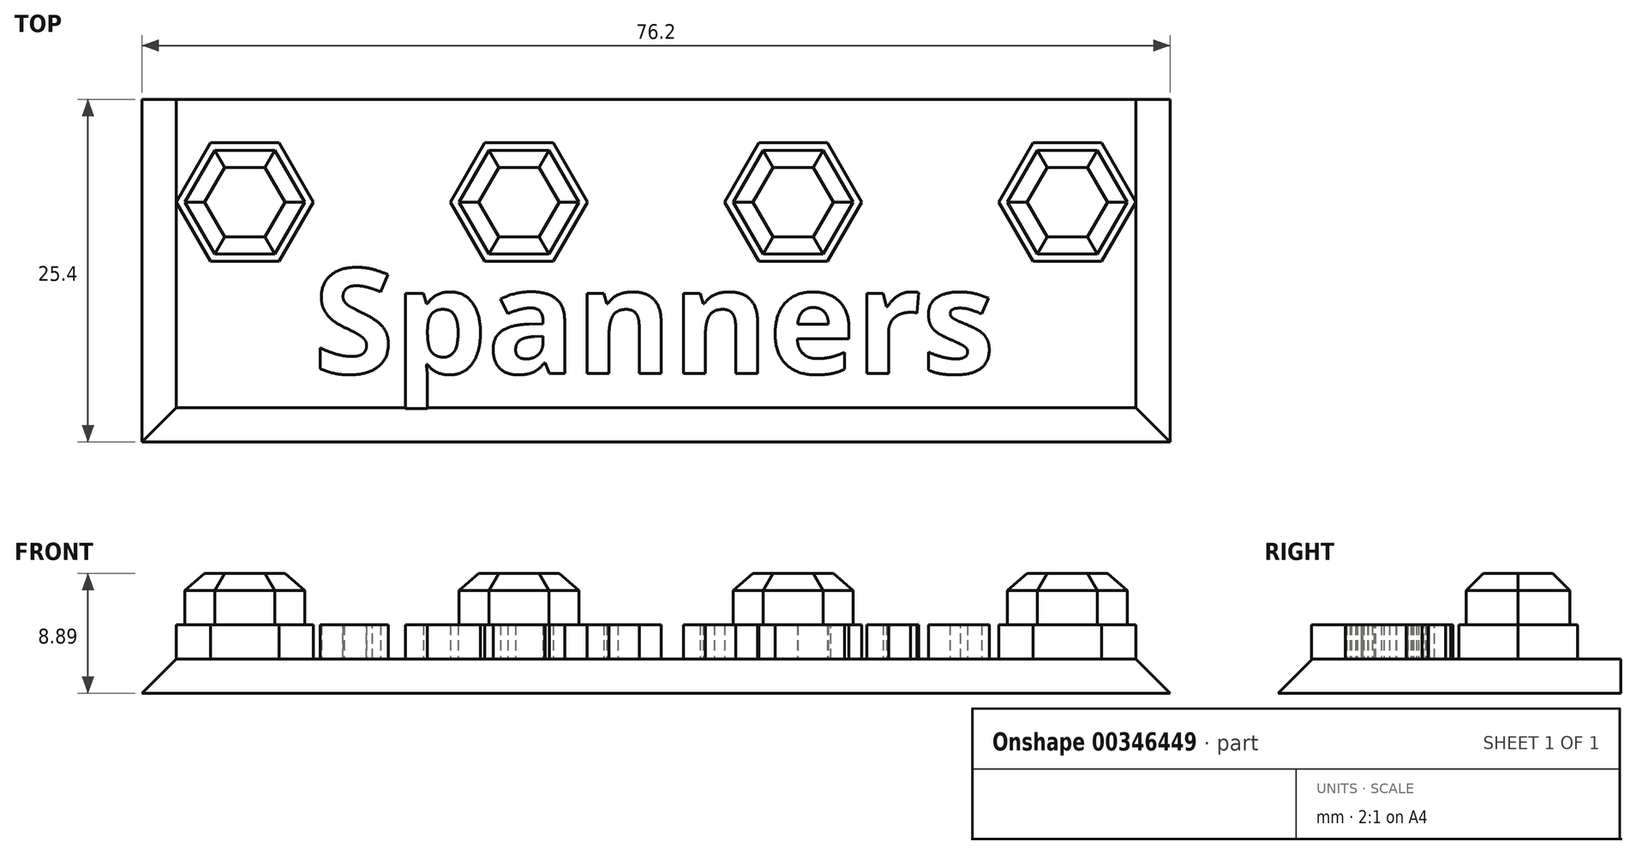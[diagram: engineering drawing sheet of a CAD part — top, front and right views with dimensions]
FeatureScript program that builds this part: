
annotation { "Feature Type Name" : "Feature", "Feature Type Description" : "" }
export const myFeature = defineFeature(function(context is Context, id is Id, definition is map)
    precondition{}
    {
        {
            var Q0;
            Q0=qCreatedBy(makeId("Top.planeOp"),FACE);
            var sketch = newSketch(context, id + "F0", { "sketchPlane" : qUnion([Q0])});
            skLineSegment(sketch, "E0.bottom", {"start": v(-52.82, 92.77) * mm, "end": v(23.38, 92.77) * mm});
            skLineSegment(sketch, "E0.top", {"start": v(-52.82, 67.37) * mm, "end": v(23.38, 67.37) * mm});
            skLineSegment(sketch, "E0.left", {"start": v(-52.82, 92.77) * mm, "end": v(-52.82, 67.37) * mm});
            skLineSegment(sketch, "E0.right", {"start": v(23.38, 92.77) * mm, "end": v(23.38, 67.37) * mm});
            skCircle(sketch, "E1.cCircle", {"center": v(-45.2, 85.15) * mm, "radius": 4.4 * mm, "construction": true});
            skLineSegment(sketch, "E1.0", {"start": v(-40.12, 85.15) * mm, "end": v(-42.66, 80.75) * mm});
            skLineSegment(sketch, "E1.1", {"start": v(-42.66, 80.75) * mm, "end": v(-47.74, 80.75) * mm});
            skLineSegment(sketch, "E1.2", {"start": v(-47.74, 80.75) * mm, "end": v(-50.28, 85.15) * mm});
            skLineSegment(sketch, "E1.3", {"start": v(-50.28, 85.15) * mm, "end": v(-47.74, 89.55) * mm});
            skLineSegment(sketch, "E1.4", {"start": v(-47.74, 89.55) * mm, "end": v(-42.66, 89.55) * mm});
            skLineSegment(sketch, "E1.5", {"start": v(-42.66, 89.55) * mm, "end": v(-40.12, 85.15) * mm});
            skPoint(sketch, "E1.0.midPoint", {"position": v(-41.39, 82.95) * mm});
            skLineSegment(sketch, "E2.1.0.0", {"start": v(-22.34, 89.55) * mm, "end": v(-19.8, 85.15) * mm});
            skLineSegment(sketch, "E2.1.0.1", {"start": v(-27.42, 89.55) * mm, "end": v(-22.34, 89.55) * mm});
            skLineSegment(sketch, "E2.1.0.2", {"start": v(-29.96, 85.15) * mm, "end": v(-27.42, 89.55) * mm});
            skLineSegment(sketch, "E2.1.0.3", {"start": v(-27.42, 80.75) * mm, "end": v(-29.96, 85.15) * mm});
            skLineSegment(sketch, "E2.1.0.4", {"start": v(-22.34, 80.75) * mm, "end": v(-27.42, 80.75) * mm});
            skLineSegment(sketch, "E2.1.0.5", {"start": v(-19.8, 85.15) * mm, "end": v(-22.34, 80.75) * mm});
            skLineSegment(sketch, "E2.2.0.0", {"start": v(-2.02, 89.55) * mm, "end": v(0.52, 85.15) * mm});
            skLineSegment(sketch, "E2.2.0.1", {"start": v(-7.1, 89.55) * mm, "end": v(-2.02, 89.55) * mm});
            skLineSegment(sketch, "E2.2.0.2", {"start": v(-9.64, 85.15) * mm, "end": v(-7.1, 89.55) * mm});
            skLineSegment(sketch, "E2.2.0.3", {"start": v(-7.1, 80.75) * mm, "end": v(-9.64, 85.15) * mm});
            skLineSegment(sketch, "E2.2.0.4", {"start": v(-2.02, 80.75) * mm, "end": v(-7.1, 80.75) * mm});
            skLineSegment(sketch, "E2.2.0.5", {"start": v(0.52, 85.15) * mm, "end": v(-2.02, 80.75) * mm});
            skLineSegment(sketch, "E2.3.0.0", {"start": v(18.3, 89.55) * mm, "end": v(20.84, 85.15) * mm});
            skLineSegment(sketch, "E2.3.0.1", {"start": v(13.22, 89.55) * mm, "end": v(18.3, 89.55) * mm});
            skLineSegment(sketch, "E2.3.0.2", {"start": v(10.68, 85.15) * mm, "end": v(13.22, 89.55) * mm});
            skLineSegment(sketch, "E2.3.0.3", {"start": v(13.22, 80.75) * mm, "end": v(10.68, 85.15) * mm});
            skLineSegment(sketch, "E2.3.0.4", {"start": v(18.3, 80.75) * mm, "end": v(13.22, 80.75) * mm});
            skLineSegment(sketch, "E2.3.0.5", {"start": v(20.84, 85.15) * mm, "end": v(18.3, 80.75) * mm});
            skLineSegment(sketch, "E2.direction1", {"start": v(-40.12, 85.15) * mm, "end": v(-19.8, 85.15) * mm, "construction": true});
            skSolve(sketch);
        }
        {
            var Q0;
            Q0=makeQuery(id+"F0.imprint","IMPRINT",FACE,{"disambiguationData":[TD([[makeQuery(id+"F0.imprint","IMPRINT",EDGE,{"derivedFrom":sQuery(id+"F0.wireOp",EDGE,"E0.bottom")}),-1.0]])]});
            extrude(context, id + "F1", {"entities" : qUnion([Q0]), "depth" : 2.54 * mm});
        }
        {
            var Q0;
            Q0=makeQuery(id+"F1.opExtrude","CAP_FACE",FACE,{"disambiguationData":[OSD([sQuery(id+"F0.wireOp",EDGE,"E0.bottom"),sQuery(id+"F0.wireOp",EDGE,"E0.top"),sQuery(id+"F0.wireOp",EDGE,"E0.left"),sQuery(id+"F0.wireOp",EDGE,"E0.right"),sQuery(id+"F0.wireOp",EDGE,"E1.0"),sQuery(id+"F0.wireOp",EDGE,"E1.1"),sQuery(id+"F0.wireOp",EDGE,"E1.2"),sQuery(id+"F0.wireOp",EDGE,"E1.3"),sQuery(id+"F0.wireOp",EDGE,"E1.4"),sQuery(id+"F0.wireOp",EDGE,"E1.5")])],"isStart":false});
            var sketch = newSketch(context, id + "F2", { "sketchPlane" : qUnion([Q0])});
            skLineSegment(sketch, "E3.0", {"start": v(-47.74, 89.55) * mm, "end": v(-42.66, 89.55) * mm});
            skLineSegment(sketch, "E3.1", {"start": v(-42.66, 89.55) * mm, "end": v(-40.12, 85.15) * mm});
            skLineSegment(sketch, "E3.2", {"start": v(-40.12, 85.15) * mm, "end": v(-42.66, 80.75) * mm});
            skLineSegment(sketch, "E3.3", {"start": v(-42.66, 80.75) * mm, "end": v(-47.74, 80.75) * mm});
            skLineSegment(sketch, "E3.4", {"start": v(-47.74, 80.75) * mm, "end": v(-50.28, 85.15) * mm});
            skLineSegment(sketch, "E3.5", {"start": v(-50.28, 85.15) * mm, "end": v(-47.74, 89.55) * mm});
            skLineSegment(sketch, "E4.0", {"start": v(-27.42, 89.55) * mm, "end": v(-22.34, 89.55) * mm});
            skLineSegment(sketch, "E4.1", {"start": v(-22.34, 89.55) * mm, "end": v(-19.8, 85.15) * mm});
            skLineSegment(sketch, "E4.2", {"start": v(-19.8, 85.15) * mm, "end": v(-22.34, 80.75) * mm});
            skLineSegment(sketch, "E4.3", {"start": v(-22.34, 80.75) * mm, "end": v(-27.42, 80.75) * mm});
            skLineSegment(sketch, "E4.4", {"start": v(-27.42, 80.75) * mm, "end": v(-29.96, 85.15) * mm});
            skLineSegment(sketch, "E4.5", {"start": v(-29.96, 85.15) * mm, "end": v(-27.42, 89.55) * mm});
            skLineSegment(sketch, "E5.0", {"start": v(-9.64, 85.15) * mm, "end": v(-7.1, 89.55) * mm});
            skLineSegment(sketch, "E5.1", {"start": v(-7.1, 89.55) * mm, "end": v(-2.02, 89.55) * mm});
            skLineSegment(sketch, "E5.2", {"start": v(-2.02, 89.55) * mm, "end": v(0.52, 85.15) * mm});
            skLineSegment(sketch, "E5.3", {"start": v(0.52, 85.15) * mm, "end": v(-2.02, 80.75) * mm});
            skLineSegment(sketch, "E5.4", {"start": v(-2.02, 80.75) * mm, "end": v(-7.1, 80.75) * mm});
            skLineSegment(sketch, "E5.5", {"start": v(-7.1, 80.75) * mm, "end": v(-9.64, 85.15) * mm});
            skLineSegment(sketch, "E6.0", {"start": v(18.3, 89.55) * mm, "end": v(20.84, 85.15) * mm});
            skLineSegment(sketch, "E6.1", {"start": v(20.84, 85.15) * mm, "end": v(18.3, 80.75) * mm});
            skLineSegment(sketch, "E6.2", {"start": v(18.3, 80.75) * mm, "end": v(13.22, 80.75) * mm});
            skLineSegment(sketch, "E6.3", {"start": v(13.22, 80.75) * mm, "end": v(10.68, 85.15) * mm});
            skLineSegment(sketch, "E6.4", {"start": v(10.68, 85.15) * mm, "end": v(13.22, 89.55) * mm});
            skLineSegment(sketch, "E6.5", {"start": v(13.22, 89.55) * mm, "end": v(18.3, 89.55) * mm});
            skSolve(sketch);
        }
        {
            var Q0;
            Q0 = qSketchRegion(id + "F2", true);
            var Q1;
            Q1=makeQuery(id+"F1.opExtrude","CAP_FACE",FACE,{"disambiguationData":[OSD([sQuery(id+"F0.wireOp",EDGE,"E0.bottom"),sQuery(id+"F0.wireOp",EDGE,"E0.top"),sQuery(id+"F0.wireOp",EDGE,"E0.left"),sQuery(id+"F0.wireOp",EDGE,"E0.right"),sQuery(id+"F0.wireOp",EDGE,"E1.0"),sQuery(id+"F0.wireOp",EDGE,"E1.1"),sQuery(id+"F0.wireOp",EDGE,"E1.2"),sQuery(id+"F0.wireOp",EDGE,"E1.3"),sQuery(id+"F0.wireOp",EDGE,"E1.4"),sQuery(id+"F0.wireOp",EDGE,"E1.5")])],"isStart":true});
            extrude(context, id + "F3", {"entities" : qUnion([Q0]), "operationType" : NewBodyOperationType.ADD, "depth" : 2.54 * mm, "hasSecondDirection" : true, "secondDirectionBound" : SecondDirectionBoundingType.UP_TO_SURFACE, "secondDirectionOppositeDirection" : true, "secondDirectionBoundEntityFace" : qUnion([Q1]), "secondDirectionDepth" : 25.4 * mm});
        }
        {
            var Q0;
            Q0=makeQuery(id+"F3.opExtrude","CAP_FACE",FACE,{"disambiguationData":[OSD([sQuery(id+"F2.wireOp",EDGE,"E3.0"),sQuery(id+"F2.wireOp",EDGE,"E3.1"),sQuery(id+"F2.wireOp",EDGE,"E3.2"),sQuery(id+"F2.wireOp",EDGE,"E3.3"),sQuery(id+"F2.wireOp",EDGE,"E3.4"),sQuery(id+"F2.wireOp",EDGE,"E3.5")])],"isStart":false});
            var sketch = newSketch(context, id + "F4", { "sketchPlane" : qUnion([Q0])});
            skLineSegment(sketch, "E7", {"start": v(-45.2, 89.55) * mm, "end": v(-45.2, 80.75) * mm});
            skCircle(sketch, "E8.cCircle", {"center": v(-45.2, 85.15) * mm, "radius": 3.85 * mm, "construction": true});
            skLineSegment(sketch, "E8.0", {"start": v(-47.42, 89) * mm, "end": v(-42.98, 89) * mm});
            skLineSegment(sketch, "E8.1", {"start": v(-42.98, 89) * mm, "end": v(-40.75, 85.15) * mm});
            skLineSegment(sketch, "E8.2", {"start": v(-40.75, 85.15) * mm, "end": v(-42.98, 81.3) * mm});
            skLineSegment(sketch, "E8.3", {"start": v(-42.98, 81.3) * mm, "end": v(-47.42, 81.3) * mm});
            skLineSegment(sketch, "E8.4", {"start": v(-47.42, 81.3) * mm, "end": v(-49.64, 85.15) * mm});
            skLineSegment(sketch, "E8.5", {"start": v(-49.64, 85.15) * mm, "end": v(-47.42, 89) * mm});
            skPoint(sketch, "E8.0.midPoint", {"position": v(-45.2, 89) * mm});
            skLineSegment(sketch, "E9.1.0.0", {"start": v(-20.43, 85.15) * mm, "end": v(-22.66, 81.3) * mm});
            skLineSegment(sketch, "E9.1.0.1", {"start": v(-22.66, 89) * mm, "end": v(-20.43, 85.15) * mm});
            skLineSegment(sketch, "E9.1.0.2", {"start": v(-27.1, 89) * mm, "end": v(-22.66, 89) * mm});
            skLineSegment(sketch, "E9.1.0.3", {"start": v(-29.32, 85.15) * mm, "end": v(-27.1, 89) * mm});
            skLineSegment(sketch, "E9.1.0.4", {"start": v(-27.1, 81.3) * mm, "end": v(-29.32, 85.15) * mm});
            skLineSegment(sketch, "E9.1.0.5", {"start": v(-22.66, 81.3) * mm, "end": v(-27.1, 81.3) * mm});
            skLineSegment(sketch, "E9.2.0.0", {"start": v(-0.11, 85.15) * mm, "end": v(-2.34, 81.3) * mm});
            skLineSegment(sketch, "E9.2.0.1", {"start": v(-2.34, 89) * mm, "end": v(-0.11, 85.15) * mm});
            skLineSegment(sketch, "E9.2.0.2", {"start": v(-6.78, 89) * mm, "end": v(-2.34, 89) * mm});
            skLineSegment(sketch, "E9.2.0.3", {"start": v(-9, 85.15) * mm, "end": v(-6.78, 89) * mm});
            skLineSegment(sketch, "E9.2.0.4", {"start": v(-6.78, 81.3) * mm, "end": v(-9, 85.15) * mm});
            skLineSegment(sketch, "E9.2.0.5", {"start": v(-2.34, 81.3) * mm, "end": v(-6.78, 81.3) * mm});
            skLineSegment(sketch, "E9.3.0.0", {"start": v(20.2, 85.15) * mm, "end": v(17.98, 81.3) * mm});
            skLineSegment(sketch, "E9.3.0.1", {"start": v(17.98, 89) * mm, "end": v(20.2, 85.15) * mm});
            skLineSegment(sketch, "E9.3.0.2", {"start": v(13.54, 89) * mm, "end": v(17.98, 89) * mm});
            skLineSegment(sketch, "E9.3.0.3", {"start": v(11.32, 85.15) * mm, "end": v(13.54, 89) * mm});
            skLineSegment(sketch, "E9.3.0.4", {"start": v(13.54, 81.3) * mm, "end": v(11.32, 85.15) * mm});
            skLineSegment(sketch, "E9.3.0.5", {"start": v(17.98, 81.3) * mm, "end": v(13.54, 81.3) * mm});
            skLineSegment(sketch, "E9.direction1", {"start": v(-42.98, 81.3) * mm, "end": v(-22.66, 81.3) * mm, "construction": true});
            skSolve(sketch);
        }
        {
            var Q0;
            Q0 = qSketchRegion(id + "F4", true);
            extrude(context, id + "F5", {"entities" : qUnion([Q0]), "operationType" : NewBodyOperationType.ADD, "depth" : 3.8 * mm});
        }
        {
            var Q0;
            Q0=makeQuery(id+"F5.opExtrude","CAP_EDGE",EDGE,{"disambiguationData":[OSD([sQuery(id+"F4.wireOp",EDGE,"E8.3")])],"isStart":false});
            var Q1;
            Q1=makeQuery(id+"F5.opExtrude","CAP_EDGE",EDGE,{"disambiguationData":[OSD([sQuery(id+"F4.wireOp",EDGE,"E8.2")])],"isStart":false});
            var Q2;
            Q2=makeQuery(id+"F5.opExtrude","CAP_EDGE",EDGE,{"disambiguationData":[OSD([sQuery(id+"F4.wireOp",EDGE,"E8.0")])],"isStart":false});
            var Q3;
            Q3=makeQuery(id+"F5.opExtrude","CAP_EDGE",EDGE,{"disambiguationData":[OSD([sQuery(id+"F4.wireOp",EDGE,"E8.5")])],"isStart":false});
            var Q4;
            Q4=makeQuery(id+"F5.opExtrude","CAP_EDGE",EDGE,{"disambiguationData":[OSD([sQuery(id+"F4.wireOp",EDGE,"E8.4")])],"isStart":false});
            var Q5;
            Q5=makeQuery(id+"F5.opExtrude","CAP_EDGE",EDGE,{"disambiguationData":[OSD([sQuery(id+"F4.wireOp",EDGE,"E8.1")])],"isStart":false});
            var Q6;
            Q6=makeQuery(id+"F5.opExtrude","CAP_EDGE",EDGE,{"disambiguationData":[OSD([sQuery(id+"F4.wireOp",EDGE,"E9.1.0.3")])],"isStart":false});
            var Q7;
            Q7=makeQuery(id+"F5.opExtrude","CAP_EDGE",EDGE,{"disambiguationData":[OSD([sQuery(id+"F4.wireOp",EDGE,"E9.1.0.2")])],"isStart":false});
            var Q8;
            Q8=makeQuery(id+"F5.opExtrude","CAP_EDGE",EDGE,{"disambiguationData":[OSD([sQuery(id+"F4.wireOp",EDGE,"E9.1.0.1")])],"isStart":false});
            var Q9;
            Q9=makeQuery(id+"F5.opExtrude","CAP_EDGE",EDGE,{"disambiguationData":[OSD([sQuery(id+"F4.wireOp",EDGE,"E9.1.0.0")])],"isStart":false});
            var Q10;
            Q10=makeQuery(id+"F5.opExtrude","CAP_EDGE",EDGE,{"disambiguationData":[OSD([sQuery(id+"F4.wireOp",EDGE,"E9.1.0.5")])],"isStart":false});
            var Q11;
            Q11=makeQuery(id+"F5.opExtrude","CAP_EDGE",EDGE,{"disambiguationData":[OSD([sQuery(id+"F4.wireOp",EDGE,"E9.1.0.4")])],"isStart":false});
            var Q12;
            Q12=makeQuery(id+"F5.opExtrude","CAP_EDGE",EDGE,{"disambiguationData":[OSD([sQuery(id+"F4.wireOp",EDGE,"E9.2.0.5")])],"isStart":false});
            var Q13;
            Q13=makeQuery(id+"F5.opExtrude","CAP_EDGE",EDGE,{"disambiguationData":[OSD([sQuery(id+"F4.wireOp",EDGE,"E9.2.0.0")])],"isStart":false});
            var Q14;
            Q14=makeQuery(id+"F5.opExtrude","CAP_EDGE",EDGE,{"disambiguationData":[OSD([sQuery(id+"F4.wireOp",EDGE,"E9.2.0.1")])],"isStart":false});
            var Q15;
            Q15=makeQuery(id+"F5.opExtrude","CAP_EDGE",EDGE,{"disambiguationData":[OSD([sQuery(id+"F4.wireOp",EDGE,"E9.2.0.2")])],"isStart":false});
            var Q16;
            Q16=makeQuery(id+"F5.opExtrude","CAP_EDGE",EDGE,{"disambiguationData":[OSD([sQuery(id+"F4.wireOp",EDGE,"E9.2.0.3")])],"isStart":false});
            var Q17;
            Q17=makeQuery(id+"F5.opExtrude","CAP_EDGE",EDGE,{"disambiguationData":[OSD([sQuery(id+"F4.wireOp",EDGE,"E9.2.0.4")])],"isStart":false});
            var Q18;
            Q18=makeQuery(id+"F5.opExtrude","CAP_EDGE",EDGE,{"disambiguationData":[OSD([sQuery(id+"F4.wireOp",EDGE,"E9.3.0.5")])],"isStart":false});
            var Q19;
            Q19=makeQuery(id+"F5.opExtrude","CAP_EDGE",EDGE,{"disambiguationData":[OSD([sQuery(id+"F4.wireOp",EDGE,"E9.3.0.4")])],"isStart":false});
            var Q20;
            Q20=makeQuery(id+"F5.opExtrude","CAP_EDGE",EDGE,{"disambiguationData":[OSD([sQuery(id+"F4.wireOp",EDGE,"E9.3.0.3")])],"isStart":false});
            var Q21;
            Q21=makeQuery(id+"F5.opExtrude","CAP_EDGE",EDGE,{"disambiguationData":[OSD([sQuery(id+"F4.wireOp",EDGE,"E9.3.0.2")])],"isStart":false});
            var Q22;
            Q22=makeQuery(id+"F5.opExtrude","CAP_EDGE",EDGE,{"disambiguationData":[OSD([sQuery(id+"F4.wireOp",EDGE,"E9.3.0.1")])],"isStart":false});
            var Q23;
            Q23=makeQuery(id+"F5.opExtrude","CAP_EDGE",EDGE,{"disambiguationData":[OSD([sQuery(id+"F4.wireOp",EDGE,"E9.3.0.0")])],"isStart":false});
            chamfer(context, id + "F6", {"entities" : qUnion([Q0, Q1, Q2, Q3, Q4, Q5, Q6, Q7, Q8, Q9, Q10, Q11, Q12, Q13, Q14, Q15, Q16, Q17, Q18, Q19, Q20, Q21, Q22, Q23]), "width" : 1.27 * mm, "tangentPropagation" : true});
        }
        {
            var Q0;
            Q0=makeQuery(id+"F1.opExtrude","CAP_EDGE",EDGE,{"disambiguationData":[OSD([sQuery(id+"F0.wireOp",EDGE,"E0.left")])],"isStart":false});
            var Q1;
            Q1=makeQuery(id+"F1.opExtrude","CAP_EDGE",EDGE,{"disambiguationData":[OSD([sQuery(id+"F0.wireOp",EDGE,"E0.top")])],"isStart":false});
            var Q2;
            Q2=makeQuery(id+"F1.opExtrude","CAP_EDGE",EDGE,{"disambiguationData":[OSD([sQuery(id+"F0.wireOp",EDGE,"E0.right")])],"isStart":false});
            chamfer(context, id + "F7", {"entities" : qUnion([Q0, Q1, Q2]), "width" : 2.54 * mm, "tangentPropagation" : true});
        }
        {
            var Q0;
            Q0=makeQuery(id+"F1.opExtrude","CAP_FACE",FACE,{"disambiguationData":[OSD([sQuery(id+"F0.wireOp",EDGE,"E0.bottom"),sQuery(id+"F0.wireOp",EDGE,"E0.top"),sQuery(id+"F0.wireOp",EDGE,"E0.left"),sQuery(id+"F0.wireOp",EDGE,"E0.right"),sQuery(id+"F0.wireOp",EDGE,"E1.0"),sQuery(id+"F0.wireOp",EDGE,"E1.1"),sQuery(id+"F0.wireOp",EDGE,"E1.2"),sQuery(id+"F0.wireOp",EDGE,"E1.3"),sQuery(id+"F0.wireOp",EDGE,"E1.4"),sQuery(id+"F0.wireOp",EDGE,"E1.5"),sQuery(id+"F0.wireOp",EDGE,"E2.1.0.0"),sQuery(id+"F0.wireOp",EDGE,"E2.1.0.1"),sQuery(id+"F0.wireOp",EDGE,"E2.1.0.2"),sQuery(id+"F0.wireOp",EDGE,"E2.1.0.3"),sQuery(id+"F0.wireOp",EDGE,"E2.1.0.4"),sQuery(id+"F0.wireOp",EDGE,"E2.1.0.5"),sQuery(id+"F0.wireOp",EDGE,"E2.2.0.0"),sQuery(id+"F0.wireOp",EDGE,"E2.2.0.1"),sQuery(id+"F0.wireOp",EDGE,"E2.2.0.2"),sQuery(id+"F0.wireOp",EDGE,"E2.2.0.3"),sQuery(id+"F0.wireOp",EDGE,"E2.2.0.4"),sQuery(id+"F0.wireOp",EDGE,"E2.2.0.5"),sQuery(id+"F0.wireOp",EDGE,"E2.3.0.0"),sQuery(id+"F0.wireOp",EDGE,"E2.3.0.1"),sQuery(id+"F0.wireOp",EDGE,"E2.3.0.2"),sQuery(id+"F0.wireOp",EDGE,"E2.3.0.3"),sQuery(id+"F0.wireOp",EDGE,"E2.3.0.4"),sQuery(id+"F0.wireOp",EDGE,"E2.3.0.5")])],"isStart":false});
            var sketch = newSketch(context, id + "F8", { "sketchPlane" : qUnion([Q0])});
            skText(sketch, "E10", { "text": "Spanners", "fontName": "OpenSans-Bold.ttf"});
            skLineSegment(sketch, "E11.0", {"start": v(-50.28, 92.77) * mm, "end": v(-50.28, 85.15) * mm});
            skLineSegment(sketch, "E12.0", {"start": v(20.84, 85.15) * mm, "end": v(20.84, 92.77) * mm});
            const initialGuessF8  = {"E10": [-0.04012, 0.07245, 1, 0, 0.00783]};
            skSetInitialGuess(sketch, initialGuessF8);
            skSolve(sketch);
        }
        {
            var Q0;
            Q0 = qSketchRegion(id + "F8", true);
            extrude(context, id + "F9", {"entities" : qUnion([Q0]), "operationType" : NewBodyOperationType.ADD, "depth" : 2.54 * mm});
        }
    });
